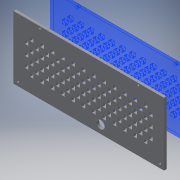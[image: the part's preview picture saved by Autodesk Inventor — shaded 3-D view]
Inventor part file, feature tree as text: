
AUTODESK INVENTOR PART (.ipt)
format: ipt  version: 2019 (Build 230136000, 136)  size: 542,720 bytes
history: native  units: mm
features: extrude x3, sketch x3, other x3, reference x2
ambient origin geometry x8: Origin, YZ Plane, XZ Plane, XY Plane, X Axis, Y Axis, Z Axis, Center Point
bodies: Volumenkörper1 (feature_tree)
feature tree (11):
  extrude  "Extrusion1"  Depth=73.0mm
  extrude  "Extrusion2"  Depth=5.0mm
  extrude  "Extrusion3"  Depth=10.0mm
  sketch  "Skizze1"  dims[d2=174.5mm d3=73.0mm]
  sketch  "Skizze2"  dims[d4=2.9mm d5=5.0mm]
  sketch  "Skizze6"  dims[d6=164.534mm d7=9.5mm d8=73.5mm d9=9.5mm d10=3.0mm d11=0.0mm d12=4.0mm d13=4.0mm d14=70.0mm d16=12.0mm d17=20.0mm d19=12.0mm d23=70.0mm d25=20.0mm d26=4.0mm d27=4.0mm d28=2.0mm d29=2.0mm d30=60.0mm d32=12.0mm d33=20.0mm d35=12.0mm d38=3.0mm d39=0.0mm d54=10.0mm d55=0.0mm]
  reference  "Referenz1"
  reference  "Referenz2"
  parser-record x1  (decoder bookkeeping rows leaked as tree rows — omitted from the tree; the rows remain in map.json)
  other  "IN-12_Nixie_Board_Zusammenbau.iam"
  other  "Gehaeuse_IN12_V1.1:1"
note: 1 file-system path scrubbed to <path> (originals preserved in map.json)
